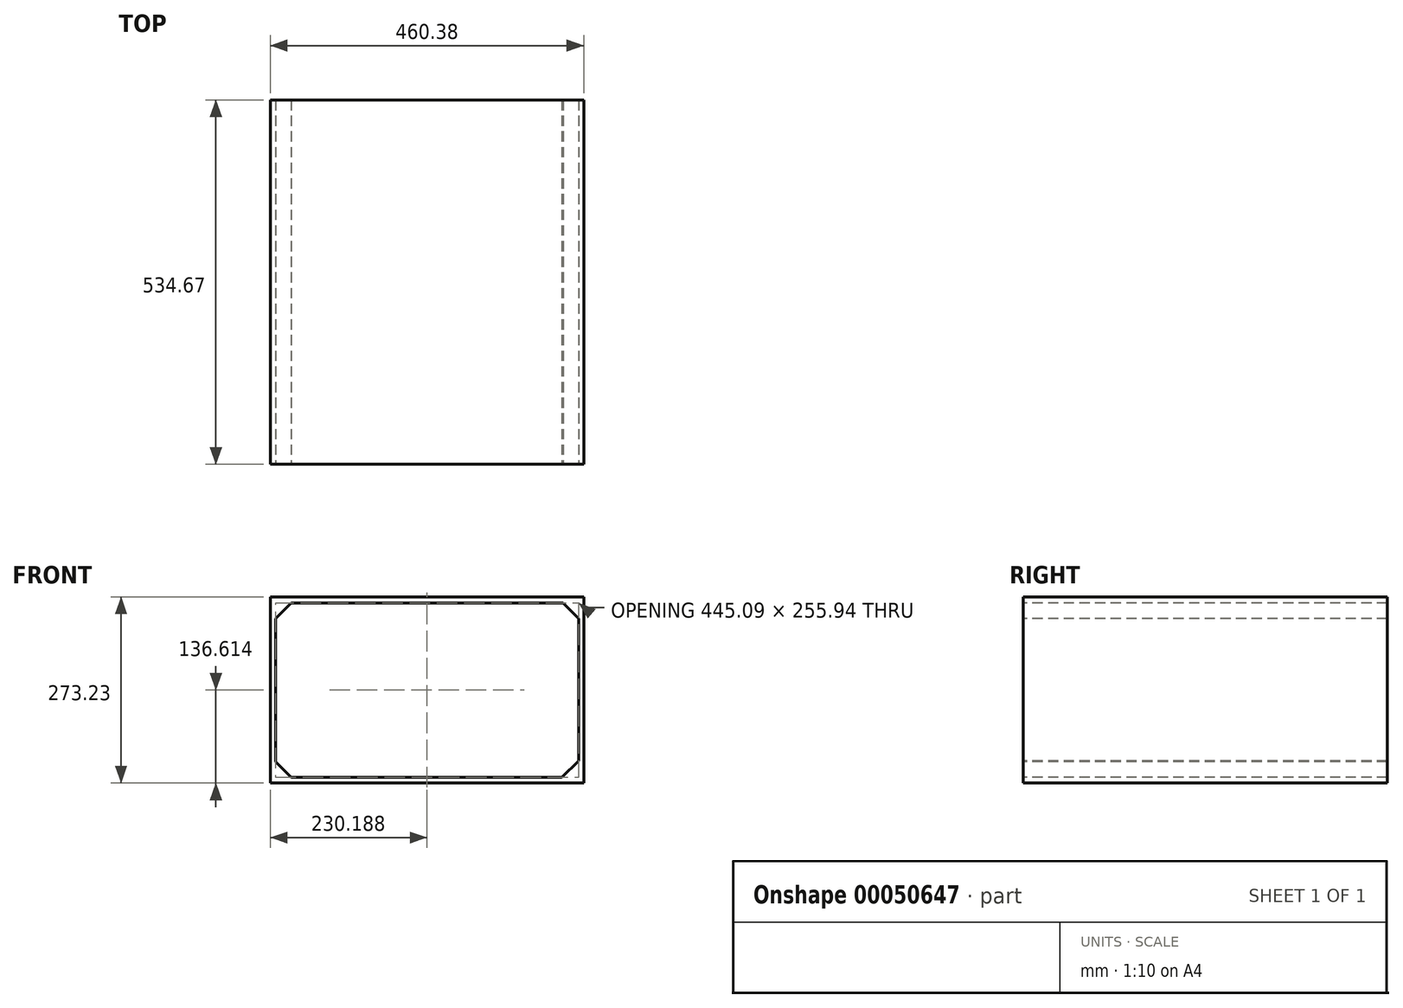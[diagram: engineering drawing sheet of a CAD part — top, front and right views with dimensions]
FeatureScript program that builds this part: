
annotation { "Feature Type Name" : "Feature", "Feature Type Description" : "" }
export const myFeature = defineFeature(function(context is Context, id is Id, definition is map)
    precondition{}
    {
        {
            var Q0;
            Q0=qCreatedBy(makeId("Top.planeOp"),FACE);
            var sketch = newSketch(context, id + "F0", { "sketchPlane" : qUnion([Q0])});
            skLineSegment(sketch, "E0.bottom", {"start": v(0, 0) * mm, "end": v(460.37, 0) * mm});
            skLineSegment(sketch, "E0.top", {"start": v(0, 534.67) * mm, "end": v(460.38, 534.67) * mm});
            skLineSegment(sketch, "E0.left", {"start": v(0, 0) * mm, "end": v(0, 534.67) * mm});
            skLineSegment(sketch, "E0.right", {"start": v(460.38, 0) * mm, "end": v(460.38, 534.67) * mm});
            skSolve(sketch);
        }
        {
            var Q0;
            Q0=makeQuery(id+"F0.imprint","IMPRINT",FACE,{"disambiguationData":[TD([[makeQuery(id+"F0.imprint","IMPRINT",EDGE,{"derivedFrom":sQuery(id+"F0.wireOp",EDGE,"E0.bottom")}),1.0]])]});
            var Q1;
            Q1 = qSketchRegion(id + "F2", true);
            extrude(context, id + "F1", {"entities" : qUnion([Q0, Q1]), "depth" : 273.23 * mm});
        }
        {
            var Q0;
            Q0=makeQuery(id+"F1.opExtrude","SWEPT_FACE",FACE,{"disambiguationData":[OSD([sQuery(id+"F0.wireOp",EDGE,"E0.bottom")])]});
            var sketch = newSketch(context, id + "F2", { "sketchPlane" : qUnion([Q0])});
            skLineSegment(sketch, "E1", {"start": v(430.01, 264.58) * mm, "end": v(452.73, 241.84) * mm});
            skLineSegment(sketch, "E2", {"start": v(7.64, 241.84) * mm, "end": v(30.36, 264.58) * mm});
            skLineSegment(sketch, "E3", {"start": v(30.36, 264.58) * mm, "end": v(430.01, 264.58) * mm});
            skLineSegment(sketch, "E4", {"start": v(7.64, 31.39) * mm, "end": v(30.36, 8.64) * mm});
            skLineSegment(sketch, "E5", {"start": v(7.64, 31.39) * mm, "end": v(7.64, 241.84) * mm});
            skLineSegment(sketch, "E6", {"start": v(427.9, 8.64) * mm, "end": v(452.73, 32.5) * mm});
            skLineSegment(sketch, "E7", {"start": v(30.36, 8.64) * mm, "end": v(427.9, 8.64) * mm});
            skLineSegment(sketch, "E8", {"start": v(452.73, 32.5) * mm, "end": v(452.73, 241.84) * mm});
            skSolve(sketch);
        }
        {
            var Q0;
            Q0=makeQuery(id+"F2.imprint","IMPRINT",FACE,{"disambiguationData":[TD([[makeQuery(id+"F2.imprint","IMPRINT",EDGE,{"derivedFrom":sQuery(id+"F2.wireOp",EDGE,"E1")}),-1.0]])]});
            extrude(context, id + "F3", {"entities" : qUnion([Q0]), "operationType" : NewBodyOperationType.REMOVE, "oppositeDirection" : true, "depth" : 536.96 * mm});
        }
    });
